# Revit family: NaughtOne_HatchandSymbolCoffeeTable
name_source: partatom
category: Furniture
units: mm (PartAtom-declared; Revit-internal decimal feet)

## family parameters
Always vertical = Yes
Cut with Voids When Loaded = No
Enable Cutting in Views = No
OmniClass Number = 23.40.20.00
OmniClass Title = General Furniture and Specialties
Render Appearance Source = Family Geometry
Room Calculation Point = No
Shared = Yes
Work Plane-Based = No

## types (2) — shared parameters
Assembly Code = E2020200
Manufacturer = Herman Miller, Inc.
Package Qty = 1
URL = http://www.hermanmiller.com
zero-valued in all types: Default Elevation

## per-type parameters (varying)
| type | Description | Lounge Height | Model | Type | Work Height |
| 16 inch table Lounge height single fabric | Hatch and Symbol Coffee Table rectangle coffee table 16 inch table Lounge height single fabric | Yes | NOSYN610L1 | 1 | No |
| 18 inch table Work height single fabric | Hatch and Symbol Coffee Table rectangle coffee table 18 inch table Work height single fabric | No | NOSYN610W1 | 2 | Yes |

## geometry (parser evidence)
native form markers: Sweep x6
no freeform markers — native parametric forms only
